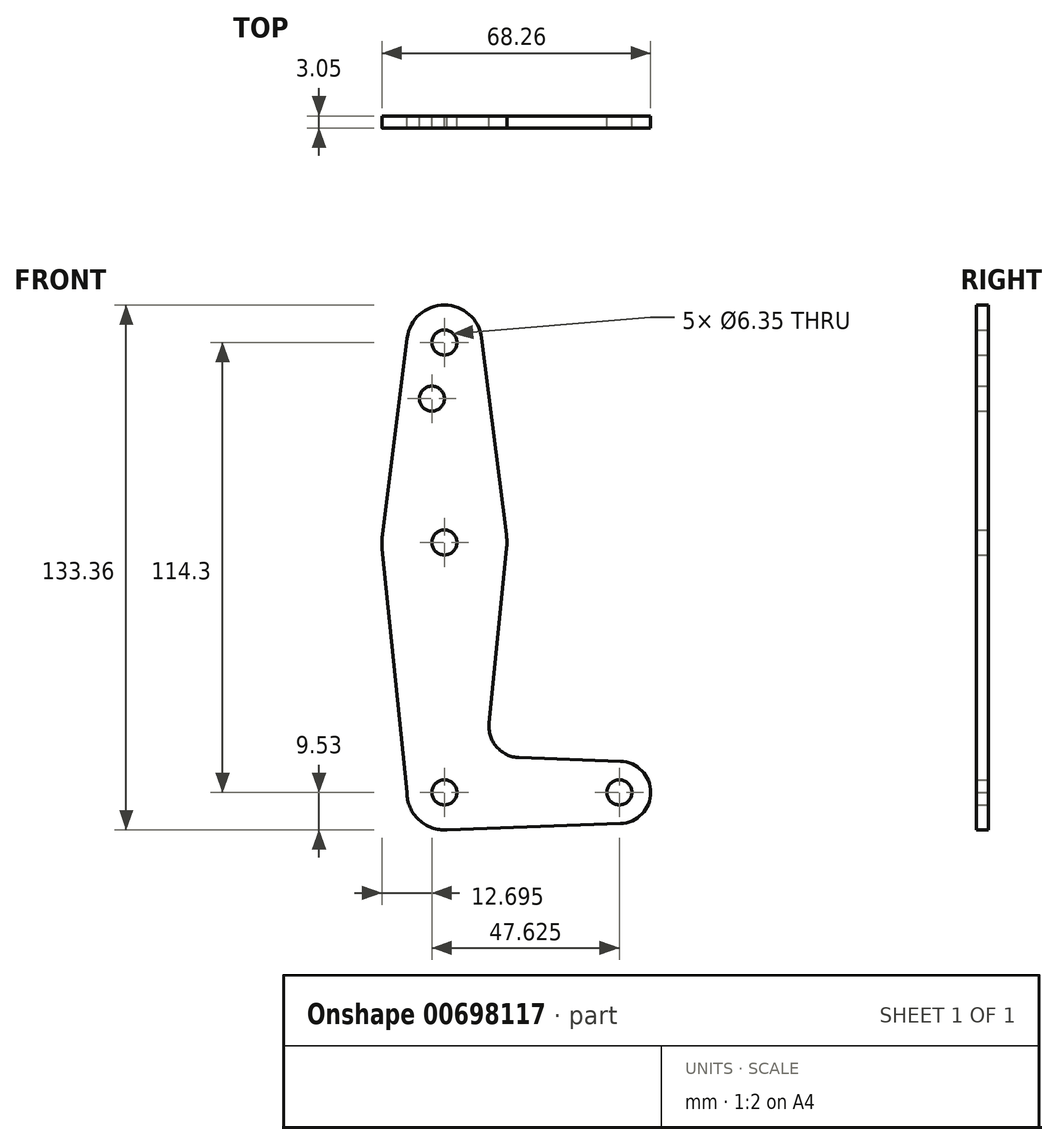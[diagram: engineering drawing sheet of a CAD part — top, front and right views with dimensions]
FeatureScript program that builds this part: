
annotation { "Feature Type Name" : "Feature", "Feature Type Description" : "" }
export const myFeature = defineFeature(function(context is Context, id is Id, definition is map)
    precondition{}
    {
        {
            var Q0;
            Q0=qCreatedBy(makeId("Front.planeOp"),FACE);
            var sketch = newSketch(context, id + "F0", { "sketchPlane" : qUnion([Q0])});
            skCircle(sketch, "E0", {"center": v(0, 0) * mm, "radius": 9.53 * mm});
            skCircle(sketch, "E1", {"center": v(44.45, 0) * mm, "radius": 7.94 * mm});
            skCircle(sketch, "E2", {"center": v(0, 114.3) * mm, "radius": 9.53 * mm});
            skCircle(sketch, "E3", {"center": v(0, 63.5) * mm, "radius": 15.88 * mm});
            skLineSegment(sketch, "E4", {"start": v(-9.45, 115.5) * mm, "end": v(-15.75, 65.48) * mm});
            skLineSegment(sketch, "E5", {"start": v(9.45, 115.5) * mm, "end": v(15.75, 65.48) * mm});
            skLineSegment(sketch, "E6", {"start": v(15.8, 61.91) * mm, "end": v(11.34, 17.59) * mm});
            skLineSegment(sketch, "E7", {"start": v(18.97, 8.85) * mm, "end": v(44.73, 7.93) * mm});
            skLineSegment(sketch, "E8", {"start": v(0, -9.53) * mm, "end": v(44.73, -7.93) * mm});
            skCircle(sketch, "E9", {"center": v(-3.18, 100.03) * mm, "radius": 3.18 * mm});
            skCircle(sketch, "E10", {"center": v(0, 114.3) * mm, "radius": 3.18 * mm});
            skCircle(sketch, "E11", {"center": v(0, 63.5) * mm, "radius": 3.18 * mm});
            skCircle(sketch, "E12", {"center": v(0, 0) * mm, "radius": 3.18 * mm});
            skCircle(sketch, "E13", {"center": v(44.45, 0) * mm, "radius": 3.18 * mm});
            skLineSegment(sketch, "E14", {"start": v(-9.53, 0) * mm, "end": v(-15.8, 61.9) * mm});
            skArc(sketch, "E15.filletArc", {"start": v(11.34, 17.59) * mm, "mid": v(13.26, 11.57) * mm, "end": v(18.97, 8.85) * mm});
            skSolve(sketch);
        }
        {
            var Q0;
            Q0 = qSketchRegion(id + "F0", true);
            extrude(context, id + "F1", {"entities" : qUnion([Q0]), "depth" : 3.05 * mm, "offsetDistance" : 25.4 * mm});
        }
    });
